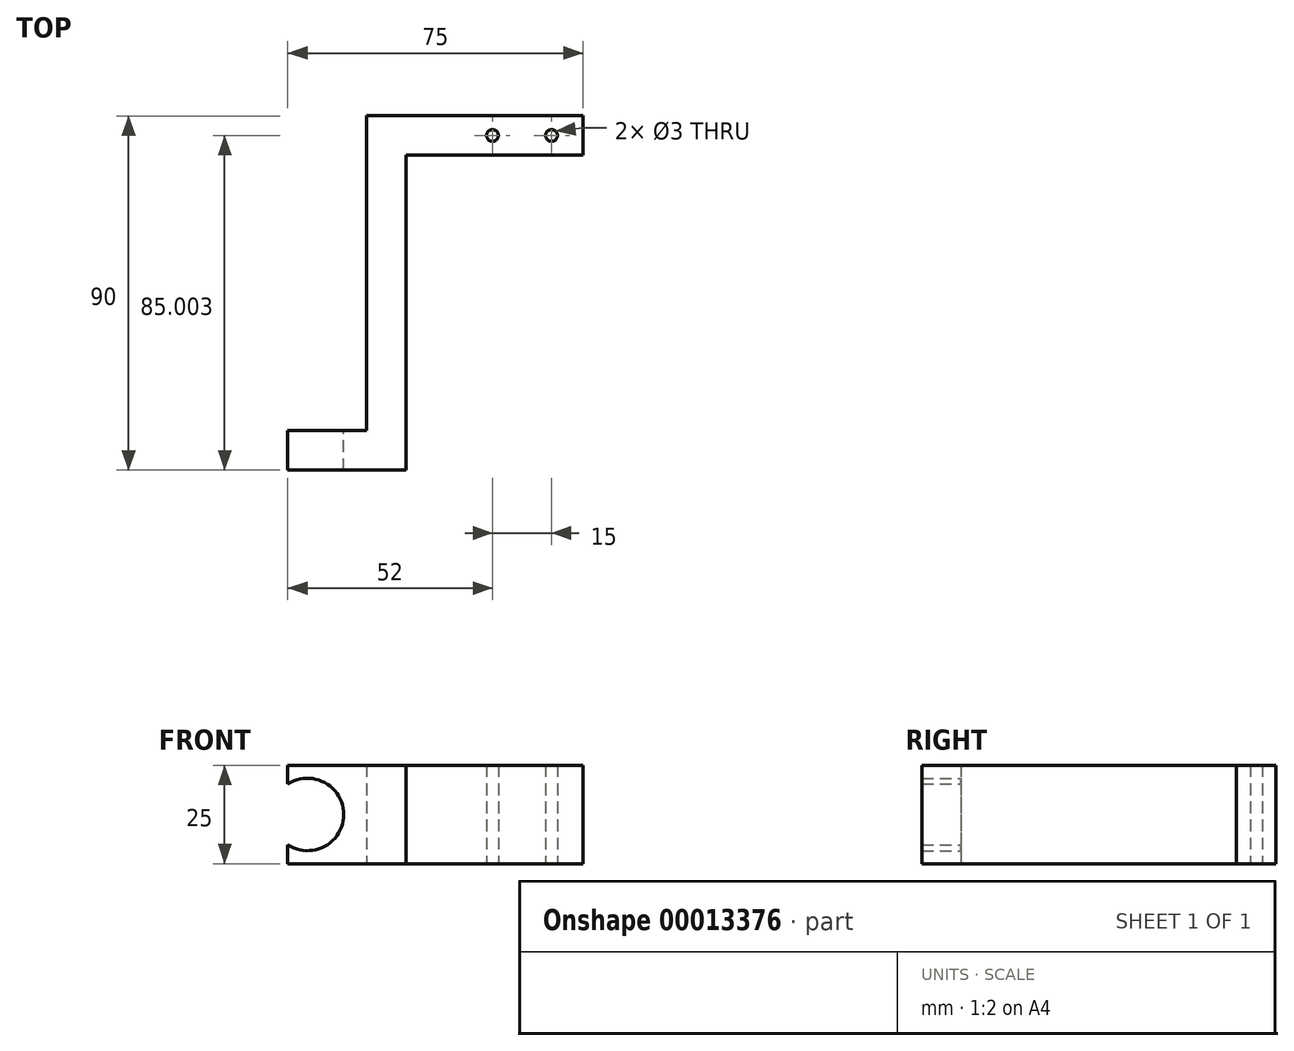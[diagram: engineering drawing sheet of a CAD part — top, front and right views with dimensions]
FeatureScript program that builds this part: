
annotation { "Feature Type Name" : "Feature", "Feature Type Description" : "" }
export const myFeature = defineFeature(function(context is Context, id is Id, definition is map)
    precondition{}
    {
        {
            var Q0;
            Q0=qCreatedBy(makeId("Top.planeOp"),FACE);
            var sketch = newSketch(context, id + "F0", { "sketchPlane" : qUnion([Q0])});
            skLineSegment(sketch, "E0", {"start": v(55, 46.61) * mm, "end": v(0, 46.61) * mm});
            skLineSegment(sketch, "E1", {"start": v(0, 46.61) * mm, "end": v(0, -33.39) * mm});
            skLineSegment(sketch, "E2", {"start": v(0, -33.39) * mm, "end": v(-20, -33.39) * mm});
            skLineSegment(sketch, "E3", {"start": v(-20, -33.39) * mm, "end": v(-20, -43.39) * mm});
            skLineSegment(sketch, "E4", {"start": v(-20, -43.39) * mm, "end": v(10, -43.39) * mm});
            skLineSegment(sketch, "E5", {"start": v(10, -43.39) * mm, "end": v(10, 36.61) * mm});
            skLineSegment(sketch, "E6", {"start": v(10, 36.61) * mm, "end": v(55, 36.61) * mm});
            skLineSegment(sketch, "E7", {"start": v(55, 36.61) * mm, "end": v(55, 46.61) * mm});
            skCircle(sketch, "E8", {"center": v(47, 41.61) * mm, "radius": 1.5 * mm});
            skCircle(sketch, "E9", {"center": v(32, 41.61) * mm, "radius": 1.5 * mm});
            skPoint(sketch, "E10", {"position": v(55, 41.61) * mm});
            skSolve(sketch);
        }
        {
            var Q0;
            {var subQ1=sQuery(id+"F0.wireOp",EDGE,"E1");Q0=makeQuery(id+"F0.imprint","IMPRINT",FACE,{"disambiguationData":[TD([[makeQuery(id+"F0.imprint","IMPRINT",EDGE,{"derivedFrom":subQ1}),1.0]])]});}
            extrude(context, id + "F1", {"entities" : qUnion([Q0]), "depth" : 25 * mm});
        }
        {
            var Q0;
            Q0=makeQuery(id+"F1.opExtrude","SWEPT_FACE",FACE,{"disambiguationData":[OSD([sQuery(id+"F0.wireOp",EDGE,"E2")])]});
            var sketch = newSketch(context, id + "F2", { "sketchPlane" : qUnion([Q0])});
            skCircle(sketch, "E11", {"center": v(15, 12.5) * mm, "radius": 9.2 * mm});
            skSolve(sketch);
        }
        {
            var Q0;
            Q0 = qSketchRegion(id + "F2", true);
            extrude(context, id + "F3", {"entities" : qUnion([Q0]), "operationType" : NewBodyOperationType.REMOVE, "oppositeDirection" : true, "depth" : 25 * mm});
        }
        {
            var Q0;
            Q0=qCreatedBy(makeId("Front.planeOp"),FACE);
            cPlane(context, id + "F4", {"entities" : qUnion([Q0]), "cplaneType" : CPlaneType.OFFSET, "offset" : 20 * mm, "width" : 150 * mm, "height" : 150 * mm});
        }
    });
